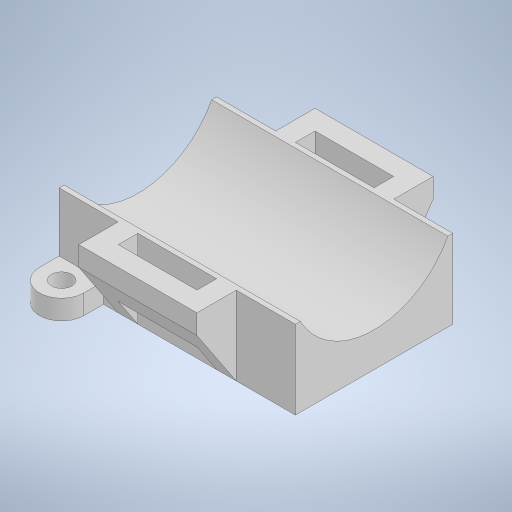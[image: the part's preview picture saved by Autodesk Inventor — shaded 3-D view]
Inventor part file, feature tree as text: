
AUTODESK INVENTOR PART (.ipt)
format: ipt  version: 2023 (Build 270158000, 158)  size: 333,824 bytes
history: native  units: in
note: dims shown in document units (in); Inventor stores cm internally (conversion verified against a paired STEP export)
features: extrude x5, sketch x5, projected_geometry x5, mirror x2
ambient origin geometry x8: Origin, YZ Plane, XZ Plane, XY Plane, X Axis, Y Axis, Z Axis, Center Point
bodies: Solid1 (feature_tree)
feature tree (17):
  extrude  "Extrusion1"  Depth=3.0in
  extrude  "Extrusion2"  Depth=1.5in
  extrude  "Extrusion3"  Depth=1.0in
  extrude  "Extrusion4"  Depth=1.0in
  mirror  "Mirror1"
  extrude  "Extrusion5"  Depth=0.25in
  mirror  "Mirror2"
  sketch  "Sketch1"  dims[d0=2.0in d1=3.0in]
  sketch  "Sketch2"  dims[d2=1.0in d3=1.5in]
  projected_geometry  "Projected Loop1"
  sketch  "Sketch3"  dims[d4=1.0in d5=0.0in d6=2.125in]
  projected_geometry  "Projected Loop2"
  sketch  "Sketch4"  dims[d7=1.0in d8=0.0in d10=1.0in]
  projected_geometry  "Projected Loop3"
  projected_geometry  "Projected Loop4"
  sketch  "Sketch5"  dims[d11=0.25in d12=0.25in d13=0.25in d14=0.25in d16=0.5in d17=1.0in d18=0.0in d19=0.25in d20=0.0in d21=0.0in d23=0.563in d24=0.25in d25=0.25in d26=0.26in d27=0.25in d28=0.2815in d29=0.25in d30=0.25in d31=0.0in]
  projected_geometry  "Projected Loop5"
